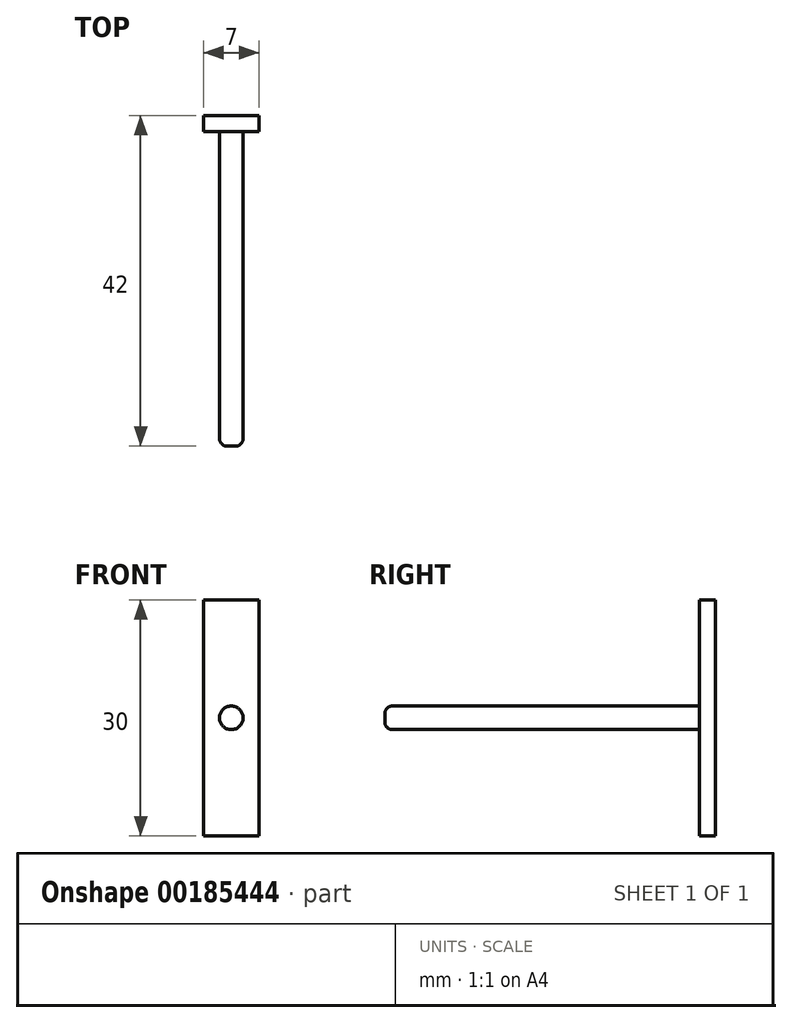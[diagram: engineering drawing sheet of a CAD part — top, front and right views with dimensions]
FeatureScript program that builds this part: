
annotation { "Feature Type Name" : "Feature", "Feature Type Description" : "" }
export const myFeature = defineFeature(function(context is Context, id is Id, definition is map)
    precondition{}
    {
        {
            var Q0;
            Q0=qCreatedBy(makeId("Front.planeOp"),FACE);
            var sketch = newSketch(context, id + "F0", { "sketchPlane" : qUnion([Q0])});
            skLineSegment(sketch, "E0.bottom", {"start": v(-3.5, 15) * mm, "end": v(3.5, 15) * mm});
            skLineSegment(sketch, "E0.top", {"start": v(-3.5, -15) * mm, "end": v(3.5, -15) * mm});
            skLineSegment(sketch, "E0.left", {"start": v(-3.5, 15) * mm, "end": v(-3.5, -15) * mm});
            skLineSegment(sketch, "E0.right", {"start": v(3.5, 15) * mm, "end": v(3.5, -15) * mm});
            skPoint(sketch, "E0.middle", {"position": v(0, 0) * mm});
            skSolve(sketch);
        }
        {
            var Q0;
            Q0 = qSketchRegion(id + "F0", true);
            extrude(context, id + "F1", {"entities" : qUnion([Q0]), "depth" : 2 * mm});
        }
        {
            var Q0;
            Q0=makeQuery(id+"F1.opExtrude","CAP_FACE",FACE,{"disambiguationData":[OSD([sQuery(id+"F0.wireOp",EDGE,"E0.bottom"),sQuery(id+"F0.wireOp",EDGE,"E0.top"),sQuery(id+"F0.wireOp",EDGE,"E0.left"),sQuery(id+"F0.wireOp",EDGE,"E0.right")])],"isStart":false});
            var sketch = newSketch(context, id + "F2", { "sketchPlane" : qUnion([Q0])});
            skCircle(sketch, "E1", {"center": v(0, 0) * mm, "radius": 1.5 * mm});
            skSolve(sketch);
        }
        {
            var Q0;
            Q0 = qSketchRegion(id + "F2", true);
            extrude(context, id + "F3", {"entities" : qUnion([Q0]), "operationType" : NewBodyOperationType.ADD, "depth" : 40 * mm});
        }
        {
            var Q0;
            Q0=makeQuery(id+"F3.opExtrude","CAP_EDGE",EDGE,{"disambiguationData":[OSD([sQuery(id+"F2.wireOp",EDGE,"E1")])],"isStart":false});
            fillet(context, id + "F4", {"entities" : qUnion([Q0]), "radius" : 1 * mm, "tangentPropagation" : true, "allowEdgeOverflow" : false});
        }
    });
